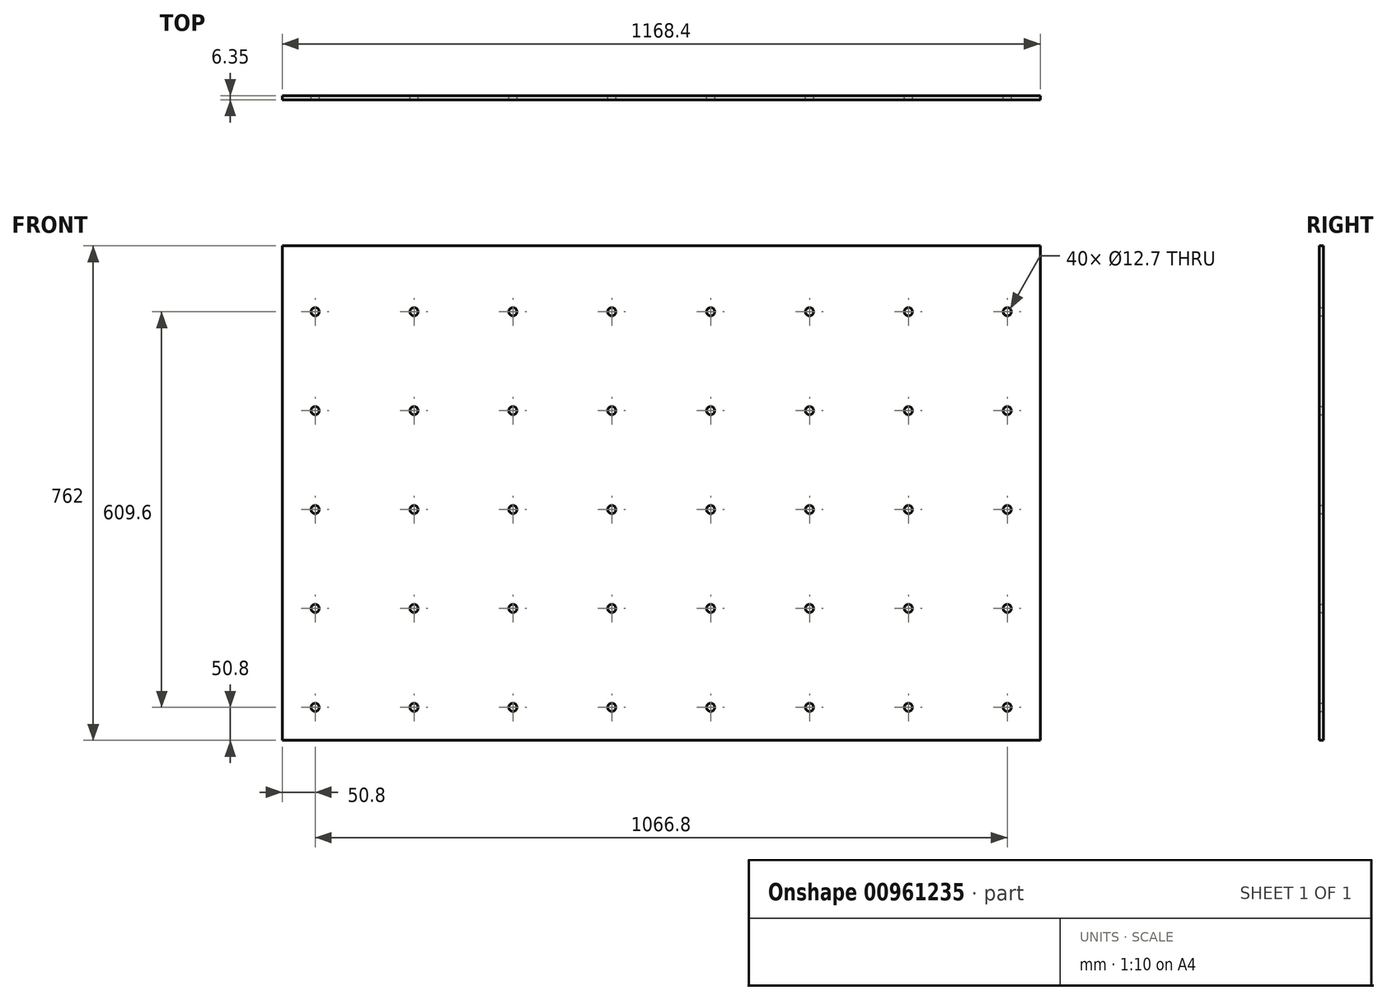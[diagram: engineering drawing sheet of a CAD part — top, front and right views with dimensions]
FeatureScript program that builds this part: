
annotation { "Feature Type Name" : "Feature", "Feature Type Description" : "" }
export const myFeature = defineFeature(function(context is Context, id is Id, definition is map)
    precondition{}
    {
        {
            var Q0;
            Q0=qCreatedBy(makeId("Front.planeOp"),FACE);
            var sketch = newSketch(context, id + "F0", { "sketchPlane" : qUnion([Q0])});
            skLineSegment(sketch, "E0.bottom", {"start": v(-609.6, 381) * mm, "end": v(558.8, 381) * mm});
            skLineSegment(sketch, "E0.top", {"start": v(-609.6, -381) * mm, "end": v(558.8, -381) * mm});
            skLineSegment(sketch, "E0.left", {"start": v(-609.6, 381) * mm, "end": v(-609.6, -381) * mm});
            skLineSegment(sketch, "E0.right", {"start": v(558.8, 381) * mm, "end": v(558.8, -381) * mm});
            skCircle(sketch, "E1", {"center": v(-558.8, -330.2) * mm, "radius": 6.35 * mm});
            skCircle(sketch, "E2", {"center": v(-558.8, -177.8) * mm, "radius": 6.35 * mm});
            skCircle(sketch, "E3", {"center": v(-558.8, -25.4) * mm, "radius": 6.35 * mm});
            skCircle(sketch, "E4", {"center": v(-558.8, 127) * mm, "radius": 6.35 * mm});
            skCircle(sketch, "E5", {"center": v(-558.8, 279.4) * mm, "radius": 6.35 * mm});
            skCircle(sketch, "E6.MirrorC", {"center": v(-406.4, 127) * mm, "radius": 6.35 * mm});
            skCircle(sketch, "E7.MirrorC", {"center": v(-406.4, 279.4) * mm, "radius": 6.35 * mm});
            skCircle(sketch, "E8.MirrorC", {"center": v(-406.4, -177.8) * mm, "radius": 6.35 * mm});
            skCircle(sketch, "E9.MirrorC", {"center": v(-406.4, -330.2) * mm, "radius": 6.35 * mm});
            skCircle(sketch, "E10.MirrorC", {"center": v(-406.4, -25.4) * mm, "radius": 6.35 * mm});
            skCircle(sketch, "E11.MirrorC", {"center": v(-101.6, 127) * mm, "radius": 6.35 * mm});
            skCircle(sketch, "E12.MirrorC", {"center": v(-101.6, 279.4) * mm, "radius": 6.35 * mm});
            skCircle(sketch, "E13.MirrorC", {"center": v(-101.6, -177.8) * mm, "radius": 6.35 * mm});
            skCircle(sketch, "E14.MirrorC", {"center": v(-101.6, -25.4) * mm, "radius": 6.35 * mm});
            skCircle(sketch, "E15.MirrorC", {"center": v(-101.6, -330.2) * mm, "radius": 6.35 * mm});
            skCircle(sketch, "E16.MirrorC", {"center": v(-254, 279.4) * mm, "radius": 6.35 * mm});
            skCircle(sketch, "E17.MirrorC", {"center": v(-254, -177.8) * mm, "radius": 6.35 * mm});
            skCircle(sketch, "E18.MirrorC", {"center": v(-254, -25.4) * mm, "radius": 6.35 * mm});
            skCircle(sketch, "E19.MirrorC", {"center": v(-254, -330.2) * mm, "radius": 6.35 * mm});
            skCircle(sketch, "E20.MirrorC", {"center": v(-254, 127) * mm, "radius": 6.35 * mm});
            skCircle(sketch, "E21.MirrorC", {"center": v(508, -25.4) * mm, "radius": 6.35 * mm});
            skCircle(sketch, "E22.MirrorC", {"center": v(508, -177.8) * mm, "radius": 6.35 * mm});
            skCircle(sketch, "E23.MirrorC", {"center": v(508, 127) * mm, "radius": 6.35 * mm});
            skCircle(sketch, "E24.MirrorC", {"center": v(508, 279.4) * mm, "radius": 6.35 * mm});
            skCircle(sketch, "E25.MirrorC", {"center": v(508, -330.2) * mm, "radius": 6.35 * mm});
            skCircle(sketch, "E26.MirrorC", {"center": v(355.6, -25.4) * mm, "radius": 6.35 * mm});
            skCircle(sketch, "E27.MirrorC", {"center": v(203.2, -177.8) * mm, "radius": 6.35 * mm});
            skCircle(sketch, "E28.MirrorC", {"center": v(50.8, 127) * mm, "radius": 6.35 * mm});
            skCircle(sketch, "E29.MirrorC", {"center": v(203.2, -330.2) * mm, "radius": 6.35 * mm});
            skCircle(sketch, "E30.MirrorC", {"center": v(203.2, 279.4) * mm, "radius": 6.35 * mm});
            skCircle(sketch, "E31.MirrorC", {"center": v(203.2, 127) * mm, "radius": 6.35 * mm});
            skCircle(sketch, "E32.MirrorC", {"center": v(50.8, -330.2) * mm, "radius": 6.35 * mm});
            skCircle(sketch, "E33.MirrorC", {"center": v(50.8, -25.4) * mm, "radius": 6.35 * mm});
            skCircle(sketch, "E34.MirrorC", {"center": v(355.6, 279.4) * mm, "radius": 6.35 * mm});
            skCircle(sketch, "E35.MirrorC", {"center": v(355.6, -330.2) * mm, "radius": 6.35 * mm});
            skCircle(sketch, "E36.MirrorC", {"center": v(355.6, 127) * mm, "radius": 6.35 * mm});
            skCircle(sketch, "E37.MirrorC", {"center": v(50.8, 279.4) * mm, "radius": 6.35 * mm});
            skCircle(sketch, "E38.MirrorC", {"center": v(203.2, -25.4) * mm, "radius": 6.35 * mm});
            skCircle(sketch, "E39.MirrorC", {"center": v(355.6, -177.8) * mm, "radius": 6.35 * mm});
            skCircle(sketch, "E40.MirrorC", {"center": v(50.8, -177.8) * mm, "radius": 6.35 * mm});
            skSolve(sketch);
        }
        {
            var Q0;
            Q0=makeQuery(id+"F0.imprint","IMPRINT",FACE,{"disambiguationData":[TD([[makeQuery(id+"F0.imprint","IMPRINT",EDGE,{"derivedFrom":sQuery(id+"F0.wireOp",EDGE,"E0.bottom")}),-1.0]])]});
            extrude(context, id + "F1", {"entities" : qUnion([Q0]), "depth" : 6.35 * mm, "offsetDistance" : 25.4 * mm});
        }
    });
